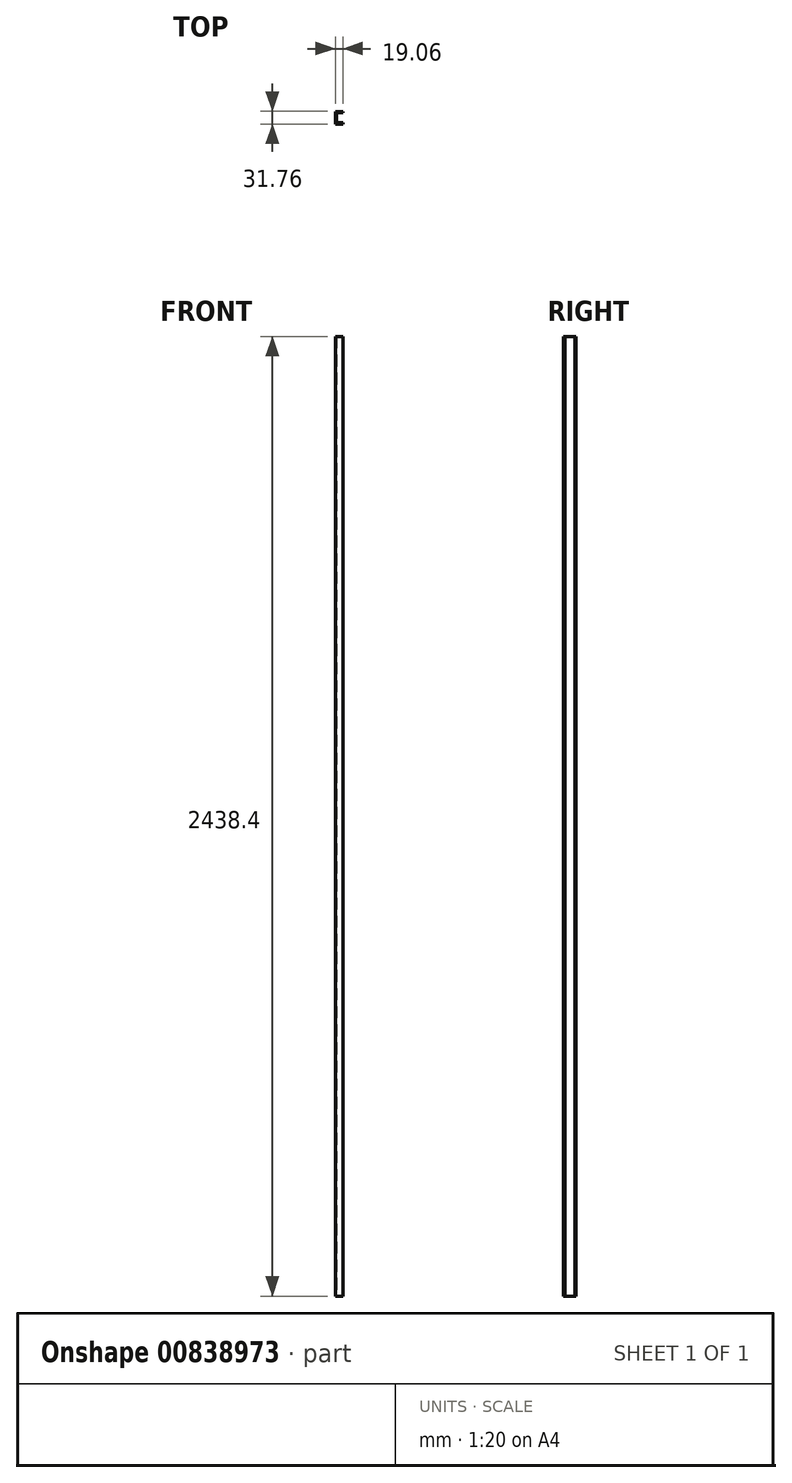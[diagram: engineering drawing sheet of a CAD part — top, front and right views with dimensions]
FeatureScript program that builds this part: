
annotation { "Feature Type Name" : "Feature", "Feature Type Description" : "" }
export const myFeature = defineFeature(function(context is Context, id is Id, definition is map)
    precondition{}
    {
        {
            var Q0;
            Q0=qCreatedBy(makeId("Top.planeOp"),FACE);
            var sketch = newSketch(context, id + "F0", { "sketchPlane" : qUnion([Q0])});
            skLineSegment(sketch, "E0.bottom", {"start": v(-9.53, 15.88) * mm, "end": v(9.53, 15.88) * mm});
            skLineSegment(sketch, "E0.top", {"start": v(-9.52, -15.88) * mm, "end": v(9.53, -15.88) * mm});
            skLineSegment(sketch, "E0.left", {"start": v(-9.52, 15.88) * mm, "end": v(-9.53, -15.88) * mm});
            skLineSegment(sketch, "E0.right", {"start": v(9.53, 15.88) * mm, "end": v(9.53, 12.7) * mm});
            skPoint(sketch, "E0.middle", {"position": v(0, 0) * mm});
            skLineSegment(sketch, "E1.bottom", {"start": v(9.52, 12.7) * mm, "end": v(-6.35, 12.7) * mm});
            skLineSegment(sketch, "E1.top", {"start": v(9.52, -12.7) * mm, "end": v(-6.35, -12.7) * mm});
            skLineSegment(sketch, "E1.right", {"start": v(-6.35, 12.7) * mm, "end": v(-6.35, -12.7) * mm});
            skPoint(sketch, "E1.middle", {"position": v(1.59, 0) * mm});
            skLineSegment(sketch, "E2.trimOffspring", {"start": v(9.52, -12.7) * mm, "end": v(9.52, -15.88) * mm});
            skSolve(sketch);
        }
        {
            var Q0;
            Q0 = qSketchRegion(id + "F0", true);
            extrude(context, id + "F1", {"entities" : qUnion([Q0]), "depth" : 2438.4 * mm, "offsetDistance" : 25.4 * mm});
        }
    });
